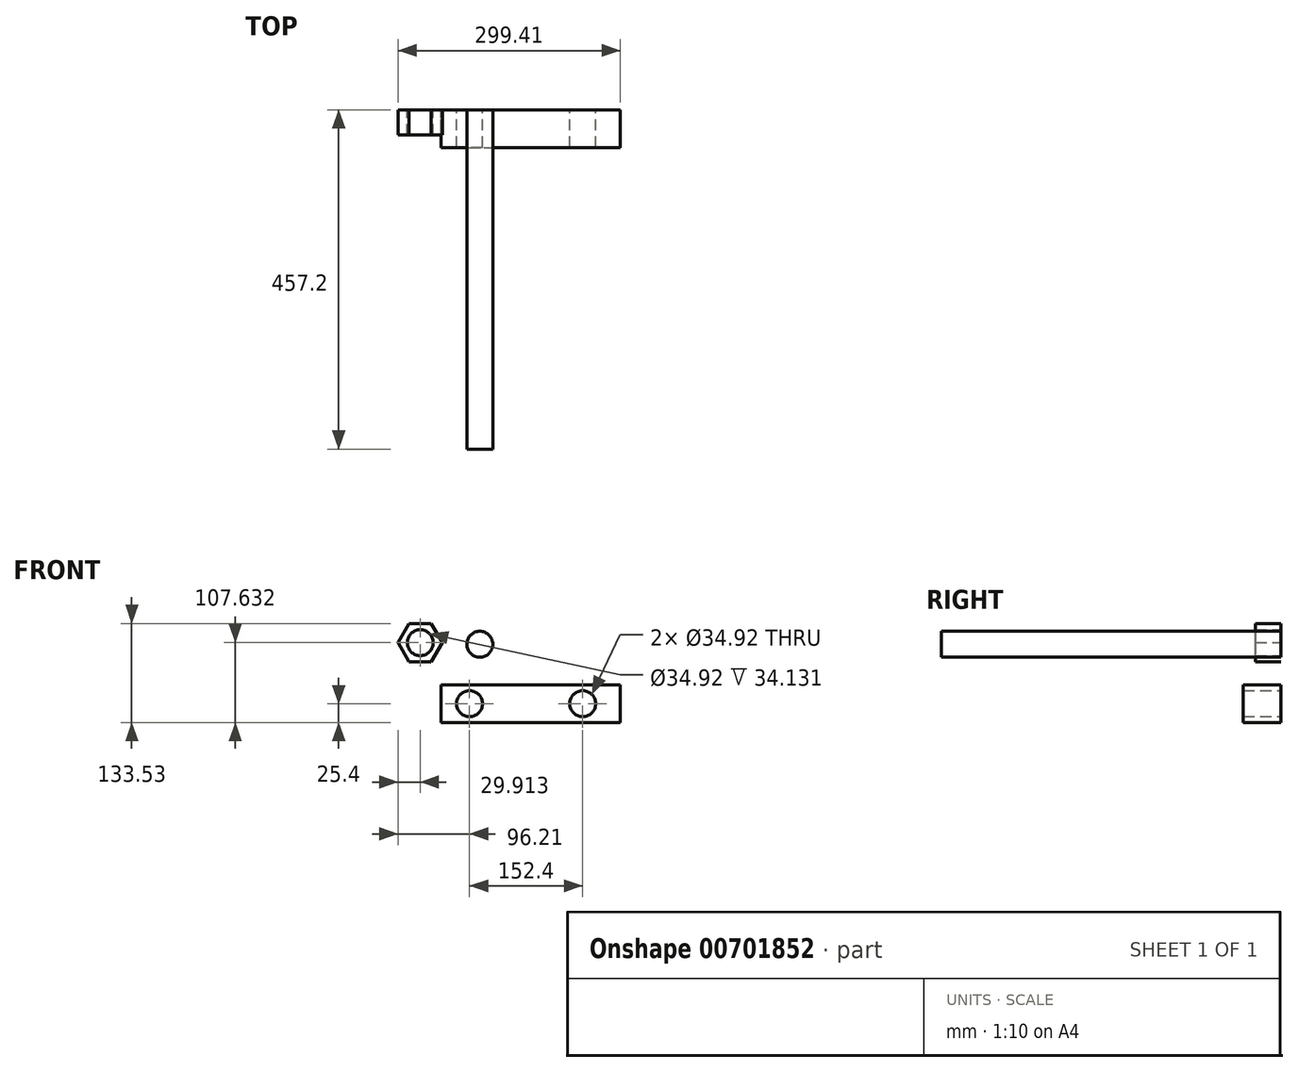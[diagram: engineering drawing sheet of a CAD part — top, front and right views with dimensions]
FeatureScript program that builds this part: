
annotation { "Feature Type Name" : "Feature", "Feature Type Description" : "" }
export const myFeature = defineFeature(function(context is Context, id is Id, definition is map)
    precondition{}
    {
        {
            var Q0;
            Q0=qCreatedBy(makeId("Front.planeOp"),FACE);
            var sketch = newSketch(context, id + "F0", { "sketchPlane" : qUnion([Q0])});
            skLineSegment(sketch, "E0.bottom", {"start": v(-114.3, -12.7) * mm, "end": v(127, -12.7) * mm});
            skLineSegment(sketch, "E0.top", {"start": v(-114.3, -63.5) * mm, "end": v(127, -63.5) * mm});
            skLineSegment(sketch, "E0.left", {"start": v(-114.3, -12.7) * mm, "end": v(-114.3, -63.5) * mm});
            skLineSegment(sketch, "E0.right", {"start": v(127, -12.7) * mm, "end": v(127, -63.5) * mm});
            skLineSegment(sketch, "E1.top", {"start": v(12.7, -63.5) * mm, "end": v(127, -63.5) * mm});
            skCircle(sketch, "E2", {"center": v(-76.2, -38.1) * mm, "radius": 17.46 * mm});
            skCircle(sketch, "E3.MirrorC", {"center": v(76.2, -38.1) * mm, "radius": 17.46 * mm});
            skSolve(sketch);
        }
        {
            var Q0;
            Q0=makeQuery(id+"F0.imprint","IMPRINT",FACE,{"disambiguationData":[TD([[makeQuery(id+"F0.imprint","IMPRINT",EDGE,{"derivedFrom":sQuery(id+"F0.wireOp",EDGE,"E0.bottom")}),-1.0]])]});
            extrude(context, id + "F1", {"entities" : qUnion([Q0]), "depth" : 50.8 * mm, "offsetDistance" : 25.4 * mm});
        }
        {
            var Q0;
            Q0=qCreatedBy(makeId("Front.planeOp"),FACE);
            var sketch = newSketch(context, id + "F2", { "sketchPlane" : qUnion([Q0])});
            skCircle(sketch, "E4", {"center": v(-142.5, 44.13) * mm, "radius": 17.46 * mm});
            skCircle(sketch, "E5", {"center": v(-142.5, 44.13) * mm, "radius": 25.9 * mm});
            skCircle(sketch, "E6.cCircle", {"center": v(-142.5, 44.13) * mm, "radius": 25.9 * mm, "construction": true});
            skLineSegment(sketch, "E6.0", {"start": v(-127.54, 18.23) * mm, "end": v(-157.45, 18.23) * mm});
            skLineSegment(sketch, "E6.1", {"start": v(-157.45, 18.23) * mm, "end": v(-172.4, 44.13) * mm});
            skLineSegment(sketch, "E6.2", {"start": v(-172.4, 44.13) * mm, "end": v(-157.45, 70.03) * mm});
            skLineSegment(sketch, "E6.3", {"start": v(-157.45, 70.03) * mm, "end": v(-127.54, 70.03) * mm});
            skLineSegment(sketch, "E6.4", {"start": v(-127.54, 70.03) * mm, "end": v(-112.59, 44.13) * mm});
            skLineSegment(sketch, "E6.5", {"start": v(-112.59, 44.13) * mm, "end": v(-127.54, 18.23) * mm});
            skPoint(sketch, "E6.0.midPoint", {"position": v(-142.5, 18.23) * mm});
            skSolve(sketch);
        }
        {
            var Q0;
            {var subQ0=sQuery(id+"F2.wireOp",EDGE,"E6.0");var subQ1=sQuery(id+"F2.wireOp",EDGE,"E5");var subQ2=makeQuery(id+"F2.imprint","INTERSECT",VERTEX,{"derivedFrom":[subQ1,subQ0]});Q0=makeQuery(id+"F2.imprint","IMPRINT",FACE,{"disambiguationData":[TD([[makeQuery(id+"F2.imprint","IMPRINT",EDGE,{"disambiguationData":[TD([[subQ2,-1.0]])],"derivedFrom":subQ1}),-1.0]])]});}
            var Q1;
            {var subQ0=sQuery(id+"F2.wireOp",EDGE,"E6.4");var subQ1=sQuery(id+"F2.wireOp",EDGE,"E5");var subQ2=makeQuery(id+"F2.imprint","INTERSECT",VERTEX,{"derivedFrom":[subQ1,subQ0]});Q1=makeQuery(id+"F2.imprint","IMPRINT",FACE,{"disambiguationData":[TD([[makeQuery(id+"F2.imprint","IMPRINT",EDGE,{"disambiguationData":[TD([[subQ2,1.0]])],"derivedFrom":subQ1}),-1.0]])]});}
            var Q2;
            {var subQ0=sQuery(id+"F2.wireOp",EDGE,"E6.3");var subQ1=sQuery(id+"F2.wireOp",EDGE,"E5");var subQ2=makeQuery(id+"F2.imprint","INTERSECT",VERTEX,{"derivedFrom":[subQ1,subQ0]});Q2=makeQuery(id+"F2.imprint","IMPRINT",FACE,{"disambiguationData":[TD([[makeQuery(id+"F2.imprint","IMPRINT",EDGE,{"disambiguationData":[TD([[subQ2,1.0]])],"derivedFrom":subQ1}),-1.0]])]});}
            var Q3;
            {var subQ0=sQuery(id+"F2.wireOp",EDGE,"E6.3");var subQ1=sQuery(id+"F2.wireOp",EDGE,"E5");var subQ2=makeQuery(id+"F2.imprint","INTERSECT",VERTEX,{"derivedFrom":[subQ1,subQ0]});Q3=makeQuery(id+"F2.imprint","IMPRINT",FACE,{"disambiguationData":[TD([[makeQuery(id+"F2.imprint","IMPRINT",EDGE,{"disambiguationData":[TD([[subQ2,-1.0]])],"derivedFrom":subQ1}),-1.0]])]});}
            var Q4;
            {var subQ0=sQuery(id+"F2.wireOp",EDGE,"E6.2");var subQ1=sQuery(id+"F2.wireOp",EDGE,"E5");var subQ2=makeQuery(id+"F2.imprint","INTERSECT",VERTEX,{"derivedFrom":[subQ1,subQ0]});Q4=makeQuery(id+"F2.imprint","IMPRINT",FACE,{"disambiguationData":[TD([[makeQuery(id+"F2.imprint","IMPRINT",EDGE,{"disambiguationData":[TD([[subQ2,-1.0]])],"derivedFrom":subQ1}),-1.0]])]});}
            var Q5;
            {var subQ0=sQuery(id+"F2.wireOp",EDGE,"E6.1");var subQ1=sQuery(id+"F2.wireOp",EDGE,"E5");var subQ2=makeQuery(id+"F2.imprint","INTERSECT",VERTEX,{"derivedFrom":[subQ1,subQ0]});Q5=makeQuery(id+"F2.imprint","IMPRINT",FACE,{"disambiguationData":[TD([[makeQuery(id+"F2.imprint","IMPRINT",EDGE,{"disambiguationData":[TD([[subQ2,-1.0]])],"derivedFrom":subQ1}),-1.0]])]});}
            var Q6;
            Q6=makeQuery(id+"F2.imprint","IMPRINT",FACE,{"disambiguationData":[TD([[makeQuery(id+"F2.imprint","IMPRINT",EDGE,{"derivedFrom":sQuery(id+"F2.wireOp",EDGE,"E4")}),-1.0]])]});
            extrude(context, id + "F3", {"entities" : qUnion([Q0, Q1, Q2, Q3, Q4, Q5, Q6]), "depth" : 34.13 * mm, "offsetDistance" : 25.4 * mm});
        }
        {
            var Q0;
            Q0=qCreatedBy(makeId("Front.planeOp"),FACE);
            var sketch = newSketch(context, id + "F4", { "sketchPlane" : qUnion([Q0])});
            skCircle(sketch, "E7", {"center": v(-62.34, 42) * mm, "radius": 17.46 * mm});
            skSolve(sketch);
        }
        {
            var Q0;
            Q0 = qSketchRegion(id + "F4", true);
            extrude(context, id + "F5", {"entities" : qUnion([Q0]), "depth" : 457.2 * mm, "offsetDistance" : 25.4 * mm});
        }
    });
